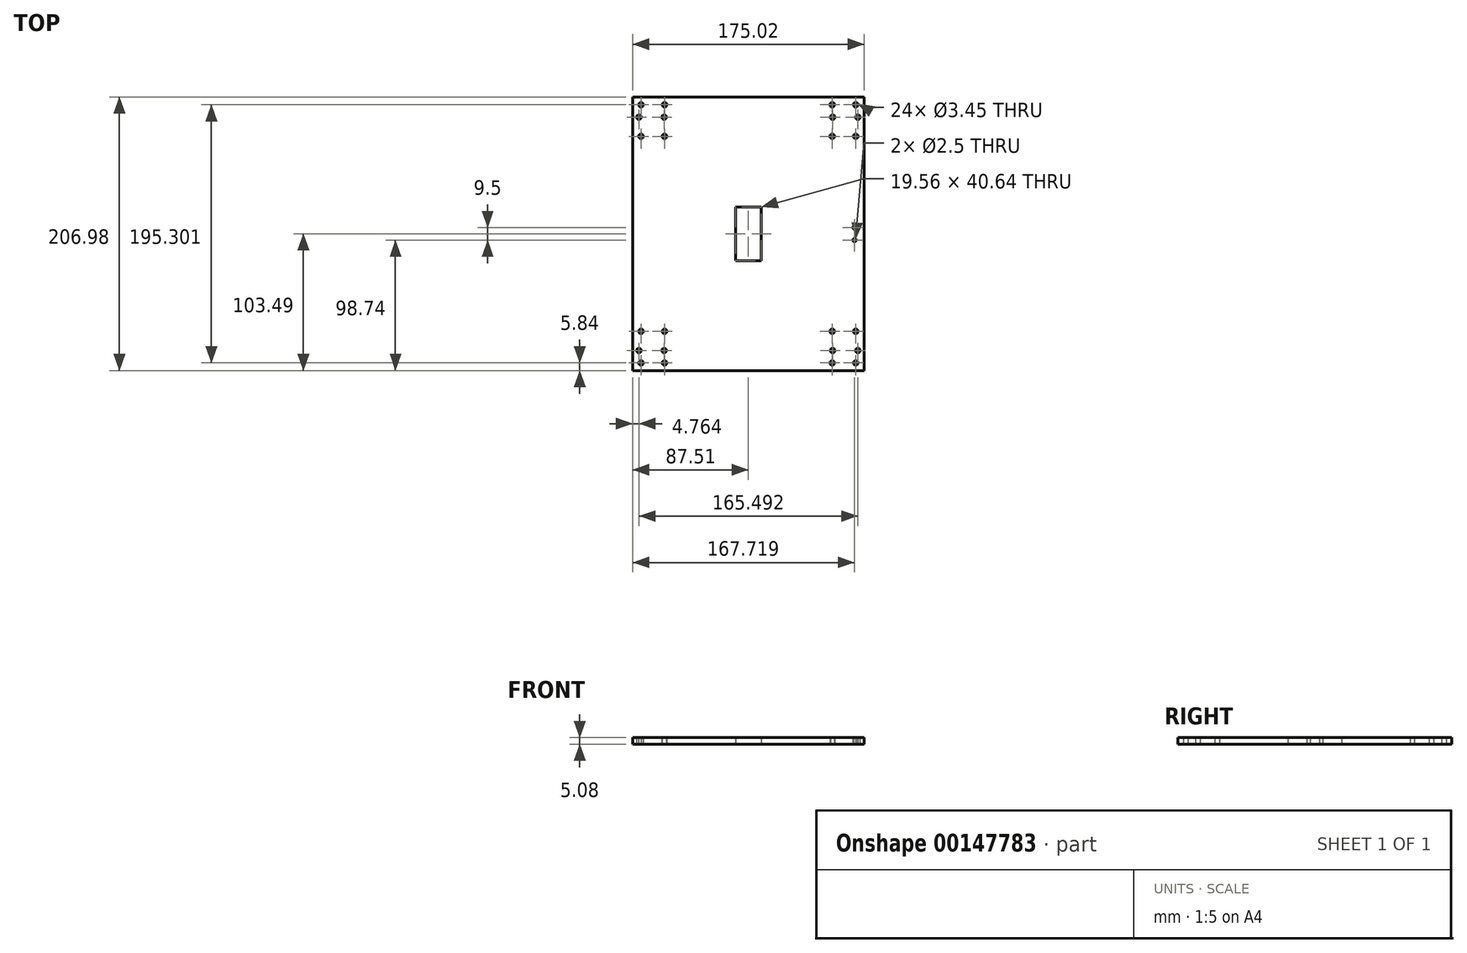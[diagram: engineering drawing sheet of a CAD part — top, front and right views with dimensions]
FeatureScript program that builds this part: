
annotation { "Feature Type Name" : "Feature", "Feature Type Description" : "" }
export const myFeature = defineFeature(function(context is Context, id is Id, definition is map)
    precondition{}
    {
        {
            var Q0;
            Q0=qCreatedBy(makeId("Top.planeOp"),FACE);
            var sketch = newSketch(context, id + "F0", { "sketchPlane" : qUnion([Q0])});
            skLineSegment(sketch, "E0.bottom", {"start": v(87.5, -103.5) * mm, "end": v(-87.5, -103.5) * mm});
            skLineSegment(sketch, "E0.top", {"start": v(87.5, 103.5) * mm, "end": v(-87.5, 103.5) * mm});
            skLineSegment(sketch, "E0.left", {"start": v(87.5, -103.5) * mm, "end": v(87.5, 103.5) * mm});
            skLineSegment(sketch, "E0.right", {"start": v(-87.5, -103.5) * mm, "end": v(-87.5, 103.5) * mm});
            skPoint(sketch, "E0.middle", {"position": v(0, 0) * mm});
            skLineSegment(sketch, "E1", {"start": v(-81.16, 103.5) * mm, "end": v(-81.16, 97.65) * mm, "construction": true});
            skLineSegment(sketch, "E2", {"start": v(-81.16, 97.65) * mm, "end": v(-87.5, 97.65) * mm, "construction": true});
            skLineSegment(sketch, "E3.bottom", {"start": v(-72.27, 85.71) * mm, "end": v(72.27, 85.71) * mm, "construction": true});
            skLineSegment(sketch, "E3.top", {"start": v(-72.27, -85.71) * mm, "end": v(72.27, -85.71) * mm, "construction": true});
            skLineSegment(sketch, "E3.left", {"start": v(-72.27, 85.71) * mm, "end": v(-72.27, -85.71) * mm, "construction": true});
            skLineSegment(sketch, "E3.right", {"start": v(72.27, 85.71) * mm, "end": v(72.27, -85.71) * mm, "construction": true});
            skLineSegment(sketch, "E4.bottom", {"start": v(-81.16, 97.65) * mm, "end": v(-63.38, 97.65) * mm, "construction": true});
            skLineSegment(sketch, "E4.top", {"start": v(-81.16, 73.77) * mm, "end": v(-63.38, 73.77) * mm, "construction": true});
            skLineSegment(sketch, "E4.left", {"start": v(-81.16, 97.65) * mm, "end": v(-81.16, 73.77) * mm, "construction": true});
            skLineSegment(sketch, "E4.right", {"start": v(-63.38, 97.65) * mm, "end": v(-63.38, 73.77) * mm, "construction": true});
            skPoint(sketch, "E4.middle", {"position": v(-72.27, 85.71) * mm});
            skLineSegment(sketch, "E5.bottom", {"start": v(81.16, 97.65) * mm, "end": v(63.38, 97.65) * mm, "construction": true});
            skLineSegment(sketch, "E5.top", {"start": v(81.16, 73.77) * mm, "end": v(63.38, 73.77) * mm, "construction": true});
            skLineSegment(sketch, "E5.left", {"start": v(81.16, 97.65) * mm, "end": v(81.16, 73.77) * mm, "construction": true});
            skLineSegment(sketch, "E5.right", {"start": v(63.38, 97.65) * mm, "end": v(63.38, 73.77) * mm, "construction": true});
            skPoint(sketch, "E5.middle", {"position": v(72.27, 85.71) * mm});
            skLineSegment(sketch, "E6.bottom", {"start": v(81.16, -97.65) * mm, "end": v(63.38, -97.65) * mm, "construction": true});
            skLineSegment(sketch, "E6.top", {"start": v(81.16, -73.77) * mm, "end": v(63.38, -73.77) * mm, "construction": true});
            skLineSegment(sketch, "E6.left", {"start": v(81.16, -97.65) * mm, "end": v(81.16, -73.77) * mm, "construction": true});
            skLineSegment(sketch, "E6.right", {"start": v(63.38, -97.65) * mm, "end": v(63.38, -73.77) * mm, "construction": true});
            skPoint(sketch, "E6.middle", {"position": v(72.27, -85.71) * mm});
            skLineSegment(sketch, "E7.bottom", {"start": v(-63.38, -97.65) * mm, "end": v(-81.16, -97.65) * mm, "construction": true});
            skLineSegment(sketch, "E7.top", {"start": v(-63.38, -73.77) * mm, "end": v(-81.16, -73.77) * mm, "construction": true});
            skLineSegment(sketch, "E7.left", {"start": v(-63.38, -97.65) * mm, "end": v(-63.38, -73.77) * mm, "construction": true});
            skLineSegment(sketch, "E7.right", {"start": v(-81.16, -97.65) * mm, "end": v(-81.16, -73.77) * mm, "construction": true});
            skPoint(sketch, "E7.middle", {"position": v(-72.27, -85.71) * mm});
            skCircle(sketch, "E8", {"center": v(-81.16, 97.65) * mm, "radius": 1.73 * mm});
            skCircle(sketch, "E9", {"center": v(-63.38, 97.65) * mm, "radius": 1.73 * mm});
            skCircle(sketch, "E10", {"center": v(-63.38, 73.77) * mm, "radius": 1.73 * mm});
            skCircle(sketch, "E11", {"center": v(-81.16, 73.77) * mm, "radius": 1.73 * mm});
            skCircle(sketch, "E12", {"center": v(81.16, 73.77) * mm, "radius": 1.73 * mm});
            skCircle(sketch, "E13", {"center": v(81.16, 97.65) * mm, "radius": 1.73 * mm});
            skCircle(sketch, "E14", {"center": v(63.38, 97.65) * mm, "radius": 1.73 * mm});
            skCircle(sketch, "E15", {"center": v(63.38, 73.77) * mm, "radius": 1.73 * mm});
            skCircle(sketch, "E16", {"center": v(81.16, -97.65) * mm, "radius": 1.73 * mm});
            skCircle(sketch, "E17", {"center": v(81.16, -73.77) * mm, "radius": 1.73 * mm});
            skCircle(sketch, "E18", {"center": v(63.38, -73.77) * mm, "radius": 1.73 * mm});
            skCircle(sketch, "E19", {"center": v(63.38, -97.65) * mm, "radius": 1.73 * mm});
            skCircle(sketch, "E20", {"center": v(-63.38, -97.65) * mm, "radius": 1.73 * mm});
            skCircle(sketch, "E21", {"center": v(-63.38, -73.77) * mm, "radius": 1.73 * mm});
            skCircle(sketch, "E22", {"center": v(-81.16, -73.77) * mm, "radius": 1.73 * mm});
            skCircle(sketch, "E23", {"center": v(-81.16, -97.65) * mm, "radius": 1.73 * mm});
            skLineSegment(sketch, "E24.bottom", {"start": v(9.78, 20.32) * mm, "end": v(-9.78, 20.32) * mm});
            skLineSegment(sketch, "E24.top", {"start": v(9.78, -20.32) * mm, "end": v(-9.78, -20.32) * mm});
            skLineSegment(sketch, "E24.left", {"start": v(9.78, 20.32) * mm, "end": v(9.78, -20.32) * mm});
            skLineSegment(sketch, "E24.right", {"start": v(-9.78, 20.32) * mm, "end": v(-9.78, -20.32) * mm});
            skLineSegment(sketch, "E25", {"start": v(87.5, 0) * mm, "end": v(80.2, 0) * mm, "construction": true});
            skLineSegment(sketch, "E26", {"start": v(80.2, 4.75) * mm, "end": v(80.2, -4.75) * mm, "construction": true});
            skCircle(sketch, "E27", {"center": v(80.2, 4.75) * mm, "radius": 1.25 * mm});
            skCircle(sketch, "E28", {"center": v(80.2, -4.75) * mm, "radius": 1.25 * mm});
            skLineSegment(sketch, "E29", {"start": v(0, -85.71) * mm, "end": v(0, -88.26) * mm, "construction": true});
            skLineSegment(sketch, "E30", {"start": v(-63.7, -88.26) * mm, "end": v(63.7, -88.26) * mm, "construction": true});
            skLineSegment(sketch, "E31", {"start": v(0, 85.71) * mm, "end": v(0, 88.26) * mm, "construction": true});
            skLineSegment(sketch, "E32", {"start": v(-63.7, 88.26) * mm, "end": v(63.7, 88.26) * mm, "construction": true});
            skLineSegment(sketch, "E33", {"start": v(-63.7, 88.26) * mm, "end": v(-82.75, 88.26) * mm, "construction": true});
            skLineSegment(sketch, "E34", {"start": v(63.7, 88.26) * mm, "end": v(82.75, 88.26) * mm, "construction": true});
            skLineSegment(sketch, "E35", {"start": v(82.75, 88.26) * mm, "end": v(87.5, 88.26) * mm, "construction": true});
            skCircle(sketch, "E36", {"center": v(63.7, 88.26) * mm, "radius": 1.73 * mm});
            skCircle(sketch, "E37", {"center": v(82.75, 88.26) * mm, "radius": 1.73 * mm});
            skLineSegment(sketch, "E38", {"start": v(-63.7, -88.26) * mm, "end": v(-82.75, -88.26) * mm, "construction": true});
            skLineSegment(sketch, "E39", {"start": v(63.7, -88.26) * mm, "end": v(82.75, -88.26) * mm, "construction": true});
            skCircle(sketch, "E40", {"center": v(-82.75, -88.26) * mm, "radius": 1.73 * mm});
            skCircle(sketch, "E41", {"center": v(-63.7, -88.26) * mm, "radius": 1.73 * mm});
            skCircle(sketch, "E42", {"center": v(-82.75, 88.26) * mm, "radius": 1.73 * mm});
            skCircle(sketch, "E43", {"center": v(-63.7, 88.26) * mm, "radius": 1.73 * mm});
            skCircle(sketch, "E44", {"center": v(63.7, -88.26) * mm, "radius": 1.73 * mm});
            skCircle(sketch, "E45", {"center": v(82.75, -88.26) * mm, "radius": 1.73 * mm});
            skSolve(sketch);
        }
        {
            var Q0;
            Q0=qSketchRegion(id+"F0",true);
            extrude(context, id + "F1", {"entities" : qUnion([Q0]), "depth" : 5.08 * mm});
        }
    });
